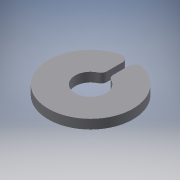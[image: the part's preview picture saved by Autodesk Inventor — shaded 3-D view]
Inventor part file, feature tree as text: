
AUTODESK INVENTOR PART (.ipt)
format: ipt  version: 2016 (Build 200138000, 138)  size: 118,272 bytes
history: native  units: mm
features: extrude x2, sketch x2, fillet x1
ambient origin geometry x8: Origin, YZ Plane, XZ Plane, XY Plane, X Axis, Y Axis, Z Axis, Center Point
bodies: Solid1 (feature_tree)
feature tree (5):
  extrude  "Extrusion1"  Depth=9.0mm
  extrude  "Extrusion2"  Depth=2.0mm
  fillet  "Fillet1"  Radius=19.5mm
  sketch  "Sketch1"  dims[d0=27.5mm d1=9.0mm]
  sketch  "Sketch2"  dims[d2=2.0mm d3=2.0mm d5=19.5mm d7=3.0mm d8=0.0mm d9=19.5mm d10=2.0mm d11=10.0mm d12=10.0mm d13=0.0mm d14=2.0mm]
